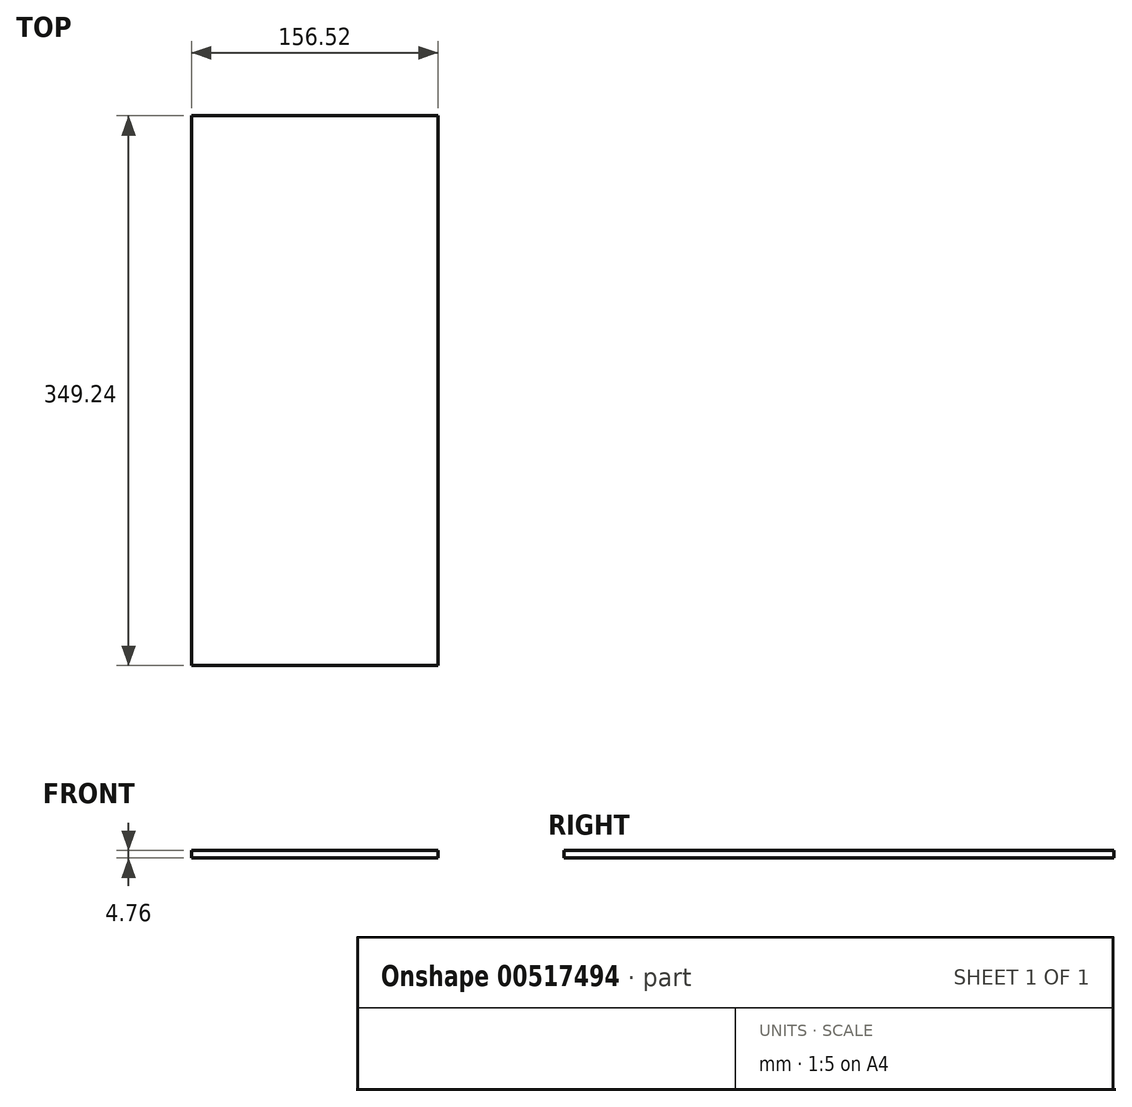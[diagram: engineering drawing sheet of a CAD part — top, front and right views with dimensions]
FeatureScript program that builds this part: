
annotation { "Feature Type Name" : "Feature", "Feature Type Description" : "" }
export const myFeature = defineFeature(function(context is Context, id is Id, definition is map)
    precondition{}
    {
        {
            var Q0;
            Q0=qCreatedBy(makeId("Top.planeOp"),FACE);
            var sketch = newSketch(context, id + "F0", { "sketchPlane" : qUnion([Q0])});
            skLineSegment(sketch, "E0.bottom", {"start": v(78.26, -174.63) * mm, "end": v(-78.26, -174.63) * mm});
            skLineSegment(sketch, "E0.top", {"start": v(78.26, 174.62) * mm, "end": v(-78.26, 174.62) * mm});
            skLineSegment(sketch, "E0.left", {"start": v(78.26, -174.63) * mm, "end": v(78.26, 174.62) * mm});
            skLineSegment(sketch, "E0.right", {"start": v(-78.26, -174.63) * mm, "end": v(-78.26, 174.62) * mm});
            skPoint(sketch, "E0.middle", {"position": v(0, 0) * mm});
            skSolve(sketch);
        }
        {
            var Q0;
            Q0=makeQuery(id+"F0.imprint","IMPRINT",FACE,{"disambiguationData":[TD([[makeQuery(id+"F0.imprint","IMPRINT",EDGE,{"derivedFrom":sQuery(id+"F0.wireOp",EDGE,"E0.bottom")}),-1.0]])]});
            extrude(context, id + "F1", {"entities" : qUnion([Q0]), "depth" : 4.76 * mm, "offsetDistance" : 25.4 * mm});
        }
    });
